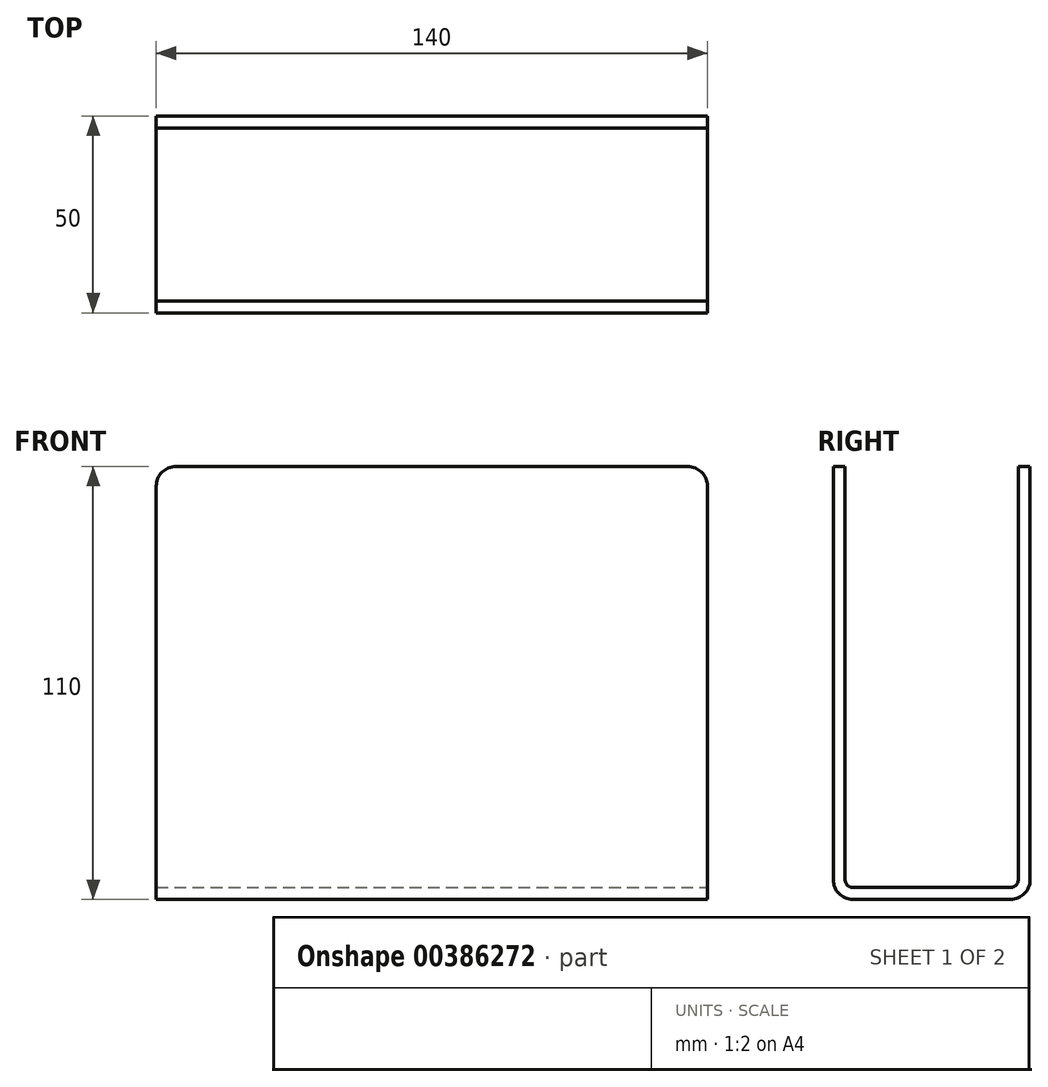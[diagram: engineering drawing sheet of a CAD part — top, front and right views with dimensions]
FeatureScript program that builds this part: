
annotation { "Feature Type Name" : "Feature", "Feature Type Description" : "" }
export const myFeature = defineFeature(function(context is Context, id is Id, definition is map)
    precondition{}
    {
        {
            var Q0;
            Q0=qCreatedBy(makeId("Top.planeOp"),FACE);
            var sketch = newSketch(context, id + "F0", { "sketchPlane" : qUnion([Q0])});
            skLineSegment(sketch, "E0.bottom", {"start": v(-72.24, -50.9) * mm, "end": v(67.76, -50.9) * mm});
            skLineSegment(sketch, "E0.top", {"start": v(-72.24, -0.9) * mm, "end": v(67.76, -0.9) * mm});
            skLineSegment(sketch, "E0.left", {"start": v(-72.24, -50.9) * mm, "end": v(-72.24, -0.9) * mm});
            skLineSegment(sketch, "E0.right", {"start": v(67.76, -50.9) * mm, "end": v(67.76, -0.9) * mm});
            skSolve(sketch);
        }
        {
            var Q0;
            Q0=makeQuery(id+"F0.imprint","IMPRINT",FACE,{"disambiguationData":[TD([[makeQuery(id+"F0.imprint","IMPRINT",EDGE,{"derivedFrom":sQuery(id+"F0.wireOp",EDGE,"E0.bottom")}),1.0]])]});
            extrude(context, id + "F1", {"entities" : qUnion([Q0]), "depth" : 110 * mm});
        }
        {
            var Q0;
            Q0=makeQuery(id+"F1.opExtrude","CAP_EDGE",EDGE,{"disambiguationData":[OSD([sQuery(id+"F0.wireOp",EDGE,"E0.left")])],"isStart":false});
            var Q1;
            Q1=makeQuery(id+"F1.opExtrude","CAP_EDGE",EDGE,{"disambiguationData":[OSD([sQuery(id+"F0.wireOp",EDGE,"E0.right")])],"isStart":false});
            var Q2;
            Q2=makeQuery(id+"F1.opExtrude","CAP_EDGE",EDGE,{"disambiguationData":[OSD([sQuery(id+"F0.wireOp",EDGE,"E0.bottom")])],"isStart":true});
            var Q3;
            Q3=makeQuery(id+"F1.opExtrude","CAP_EDGE",EDGE,{"disambiguationData":[OSD([sQuery(id+"F0.wireOp",EDGE,"E0.top")])],"isStart":true});
            fillet(context, id + "F2", {"entities" : qUnion([Q0, Q1, Q2, Q3]), "radius" : 5 * mm, "tangentPropagation" : true, "allowEdgeOverflow" : false});
        }
        {
            var Q0;
            Q0=makeQuery(id+"F1.opExtrude","SWEPT_FACE",FACE,{"disambiguationData":[OSD([sQuery(id+"F0.wireOp",EDGE,"E0.right")])]});
            var Q1;
            Q1=makeQuery(id+"F2.opFillet","BLEND_FACE",FACE,{"disambiguationData":[OSD([sQuery(id+"F0.wireOp",EDGE,"E0.right")])]});
            var Q2;
            Q2=makeQuery(id+"F1.opExtrude","CAP_FACE",FACE,{"disambiguationData":[OSD([sQuery(id+"F0.wireOp",EDGE,"E0.bottom"),sQuery(id+"F0.wireOp",EDGE,"E0.top"),sQuery(id+"F0.wireOp",EDGE,"E0.left"),sQuery(id+"F0.wireOp",EDGE,"E0.right")])],"isStart":false});
            var Q3;
            Q3=makeQuery(id+"F2.opFillet","BLEND_FACE",FACE,{"disambiguationData":[OSD([sQuery(id+"F0.wireOp",EDGE,"E0.left")])]});
            var Q4;
            Q4=makeQuery(id+"F1.opExtrude","SWEPT_FACE",FACE,{"disambiguationData":[OSD([sQuery(id+"F0.wireOp",EDGE,"E0.left")])]});
            shell(context, id + "F3", {"entities" : qUnion([Q0, Q1, Q2, Q3, Q4]), "thickness" : 3 * mm});
        }
    });
